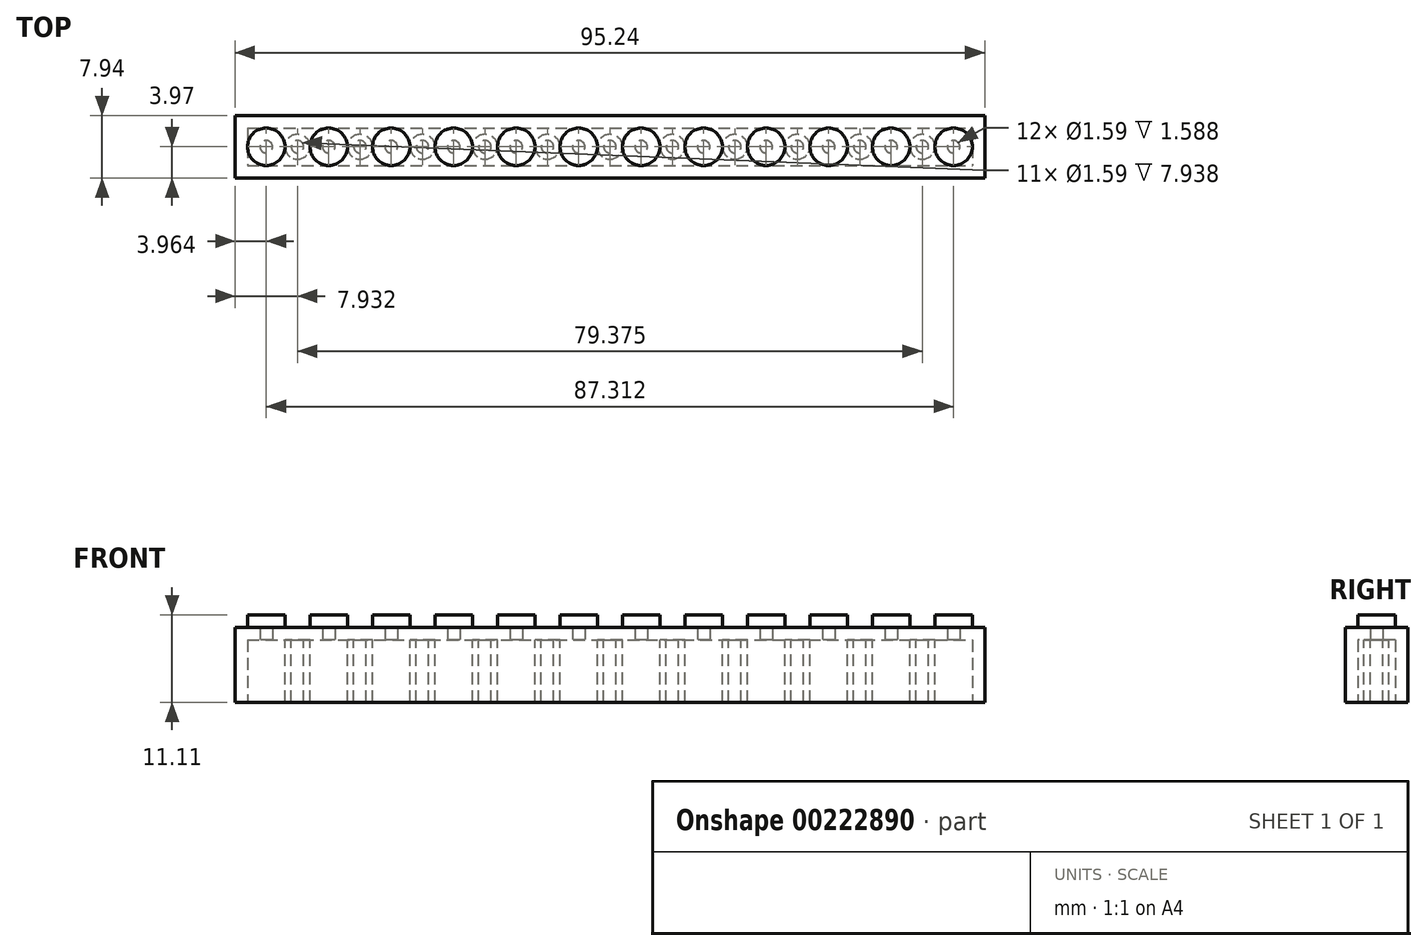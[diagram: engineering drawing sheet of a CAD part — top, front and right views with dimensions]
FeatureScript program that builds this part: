
annotation { "Feature Type Name" : "Feature", "Feature Type Description" : "" }
export const myFeature = defineFeature(function(context is Context, id is Id, definition is map)
    precondition{}
    {
        {
            var Q0;
            Q0=qCreatedBy(makeId("Top.planeOp"),FACE);
            var sketch = newSketch(context, id + "F0", { "sketchPlane" : qUnion([Q0])});
            skLineSegment(sketch, "E0.bottom", {"start": v(-47.63, 3.97) * mm, "end": v(47.62, 3.97) * mm});
            skLineSegment(sketch, "E0.top", {"start": v(-47.63, -3.97) * mm, "end": v(47.63, -3.97) * mm});
            skLineSegment(sketch, "E0.left", {"start": v(-47.63, 3.97) * mm, "end": v(-47.63, -3.97) * mm});
            skLineSegment(sketch, "E0.right", {"start": v(47.62, 3.97) * mm, "end": v(47.62, -3.97) * mm});
            skPoint(sketch, "E0.middle", {"position": v(0, 0) * mm});
            skCircle(sketch, "E1", {"center": v(-43.66, 0) * mm, "radius": 2.38 * mm});
            skCircle(sketch, "E2.1.0.0", {"center": v(-35.72, 0) * mm, "radius": 2.38 * mm});
            skCircle(sketch, "E2.2.0.0", {"center": v(-27.78, 0) * mm, "radius": 2.38 * mm});
            skCircle(sketch, "E2.3.0.0", {"center": v(-19.84, 0) * mm, "radius": 2.38 * mm});
            skLineSegment(sketch, "E2.direction1", {"start": v(-43.66, 0) * mm, "end": v(-35.72, 0) * mm, "construction": true});
            skCircle(sketch, "E3.0.4.0", {"center": v(-11.9, 0) * mm, "radius": 2.38 * mm});
            skCircle(sketch, "E3.0.5.0", {"center": v(-3.97, 0) * mm, "radius": 2.38 * mm});
            skCircle(sketch, "E4.0.6.0", {"center": v(3.97, 0) * mm, "radius": 2.38 * mm});
            skCircle(sketch, "E4.0.7.0", {"center": v(11.9, 0) * mm, "radius": 2.38 * mm});
            skCircle(sketch, "E4.0.8.0", {"center": v(19.84, 0) * mm, "radius": 2.38 * mm});
            skCircle(sketch, "E4.0.9.0", {"center": v(27.78, 0) * mm, "radius": 2.38 * mm});
            skCircle(sketch, "E4.0.10.0", {"center": v(35.72, 0) * mm, "radius": 2.38 * mm});
            skCircle(sketch, "E4.0.11.0", {"center": v(43.66, 0) * mm, "radius": 2.38 * mm});
            skSolve(sketch);
        }
        {
            var Q0;
            Q0=makeQuery(id+"F0.imprint","IMPRINT",FACE,{"disambiguationData":[TD([[makeQuery(id+"F0.imprint","IMPRINT",EDGE,{"derivedFrom":sQuery(id+"F0.wireOp",EDGE,"E0.bottom")}),-1.0]])]});
            extrude(context, id + "F1", {"entities" : qUnion([Q0]), "depth" : 9.52 * mm});
        }
        {
            var Q0;
            Q0=makeQuery(id+"F0.imprint","IMPRINT",FACE,{"disambiguationData":[TD([[makeQuery(id+"F0.imprint","IMPRINT",EDGE,{"derivedFrom":sQuery(id+"F0.wireOp",EDGE,"8b71ed98-f0e1-4300-85cb-82ad82c44b3e0.MirrorC")}),-1.0]])]});
            var Q1;
            Q1=makeQuery(id+"F0.imprint","IMPRINT",FACE,{"disambiguationData":[TD([[makeQuery(id+"F0.imprint","IMPRINT",EDGE,{"derivedFrom":sQuery(id+"F0.wireOp",EDGE,"E1")}),1.0]])]});
            var Q2;
            Q2=makeQuery(id+"F0.imprint","IMPRINT",FACE,{"disambiguationData":[TD([[makeQuery(id+"F0.imprint","IMPRINT",EDGE,{"derivedFrom":sQuery(id+"F0.wireOp",EDGE,"E2.1.0.0")}),1.0]])]});
            var Q3;
            Q3=makeQuery(id+"F0.imprint","IMPRINT",FACE,{"disambiguationData":[TD([[makeQuery(id+"F0.imprint","IMPRINT",EDGE,{"derivedFrom":sQuery(id+"F0.wireOp",EDGE,"E2.2.0.0")}),1.0]])]});
            var Q4;
            Q4=makeQuery(id+"F0.imprint","IMPRINT",FACE,{"disambiguationData":[TD([[makeQuery(id+"F0.imprint","IMPRINT",EDGE,{"derivedFrom":sQuery(id+"F0.wireOp",EDGE,"E2.3.0.0")}),1.0]])]});
            var Q5;
            Q5=makeQuery(id+"F0.imprint","IMPRINT",FACE,{"disambiguationData":[TD([[makeQuery(id+"F0.imprint","IMPRINT",EDGE,{"derivedFrom":sQuery(id+"F0.wireOp",EDGE,"E3.0.4.0")}),1.0]])]});
            var Q6;
            Q6=makeQuery(id+"F0.imprint","IMPRINT",FACE,{"disambiguationData":[TD([[makeQuery(id+"F0.imprint","IMPRINT",EDGE,{"derivedFrom":sQuery(id+"F0.wireOp",EDGE,"E3.0.5.0")}),1.0]])]});
            var Q7;
            Q7=makeQuery(id+"F0.imprint","IMPRINT",FACE,{"disambiguationData":[TD([[makeQuery(id+"F0.imprint","IMPRINT",EDGE,{"derivedFrom":sQuery(id+"F0.wireOp",EDGE,"E4.0.6.0")}),1.0]])]});
            var Q8;
            Q8=makeQuery(id+"F0.imprint","IMPRINT",FACE,{"disambiguationData":[TD([[makeQuery(id+"F0.imprint","IMPRINT",EDGE,{"derivedFrom":sQuery(id+"F0.wireOp",EDGE,"E4.0.7.0")}),1.0]])]});
            var Q9;
            Q9=makeQuery(id+"F0.imprint","IMPRINT",FACE,{"disambiguationData":[TD([[makeQuery(id+"F0.imprint","IMPRINT",EDGE,{"derivedFrom":sQuery(id+"F0.wireOp",EDGE,"E4.0.8.0")}),1.0]])]});
            var Q10;
            Q10=makeQuery(id+"F0.imprint","IMPRINT",FACE,{"disambiguationData":[TD([[makeQuery(id+"F0.imprint","IMPRINT",EDGE,{"derivedFrom":sQuery(id+"F0.wireOp",EDGE,"E4.0.9.0")}),1.0]])]});
            var Q11;
            Q11=makeQuery(id+"F0.imprint","IMPRINT",FACE,{"disambiguationData":[TD([[makeQuery(id+"F0.imprint","IMPRINT",EDGE,{"derivedFrom":sQuery(id+"F0.wireOp",EDGE,"E4.0.10.0")}),1.0]])]});
            var Q12;
            Q12=makeQuery(id+"F0.imprint","IMPRINT",FACE,{"disambiguationData":[TD([[makeQuery(id+"F0.imprint","IMPRINT",EDGE,{"derivedFrom":sQuery(id+"F0.wireOp",EDGE,"E4.0.11.0")}),1.0]])]});
            extrude(context, id + "F2", {"entities" : qUnion([Q0, Q1, Q2, Q3, Q4, Q5, Q6, Q7, Q8, Q9, Q10, Q11, Q12]), "operationType" : NewBodyOperationType.ADD, "depth" : 11.1 * mm});
        }
        {
            var Q0;
            {var subQ0=sQuery(id+"F0.wireOp",EDGE,"8b71ed98-f0e1-4300-85cb-82ad82c44b3e0.MirrorC");var subQ1=sQuery(id+"F0.wireOp",EDGE,"E1");Q0=makeQuery(id+"F2.boolean.opBoolean","MERGE",FACE,{"derivedFrom":[makeQuery(id+"F1.opExtrude","CAP_FACE",FACE,{"disambiguationData":[OSD([sQuery(id+"F0.wireOp",EDGE,"E0.bottom"),sQuery(id+"F0.wireOp",EDGE,"E0.top"),sQuery(id+"F0.wireOp",EDGE,"E0.left"),sQuery(id+"F0.wireOp",EDGE,"E0.right"),subQ1,subQ0])],"isStart":true}),makeQuery(id+"F2.opExtrude","CAP_FACE",FACE,{"disambiguationData":[OSD([subQ1])],"isStart":true}),makeQuery(id+"F2.opExtrude","CAP_FACE",FACE,{"disambiguationData":[OSD([subQ0])],"isStart":true})]});}
            shell(context, id + "F3", {"entities" : qUnion([Q0]), "thickness" : 1.59 * mm});
        }
        {
            var Q0;
            Q0=makeQuery(id+"F3.opShell","OFFSET_FACE",FACE,{"disambiguationData":[OSD([sQuery(id+"F0.wireOp",EDGE,"E0.bottom"),sQuery(id+"F0.wireOp",EDGE,"E0.top"),sQuery(id+"F0.wireOp",EDGE,"E0.left"),sQuery(id+"F0.wireOp",EDGE,"E0.right"),sQuery(id+"F0.wireOp",EDGE,"E1"),sQuery(id+"F0.wireOp",EDGE,"8b71ed98-f0e1-4300-85cb-82ad82c44b3e0.MirrorC")])]});
            var sketch = newSketch(context, id + "F4", { "sketchPlane" : qUnion([Q0])});
            skCircle(sketch, "E5", {"center": v(-39.69, 0) * mm, "radius": 1.59 * mm});
            skCircle(sketch, "E6", {"center": v(-39.69, 0) * mm, "radius": 0.8 * mm});
            skLineSegment(sketch, "E7.direction1", {"start": v(-39.69, 0) * mm, "end": v(-31.75, 0) * mm, "construction": true});
            skCircle(sketch, "E8.0.1.0", {"center": v(-31.75, 0) * mm, "radius": 1.59 * mm});
            skCircle(sketch, "E8.2.1.0", {"center": v(-31.75, 0) * mm, "radius": 0.8 * mm});
            skCircle(sketch, "E8.0.2.0", {"center": v(-23.81, 0) * mm, "radius": 1.59 * mm});
            skCircle(sketch, "E8.2.2.0", {"center": v(-23.81, 0) * mm, "radius": 0.8 * mm});
            skCircle(sketch, "E8.0.3.0", {"center": v(-15.88, 0) * mm, "radius": 1.59 * mm});
            skCircle(sketch, "E8.2.3.0", {"center": v(-15.88, 0) * mm, "radius": 0.8 * mm});
            skCircle(sketch, "E8.0.4.0", {"center": v(-7.94, 0) * mm, "radius": 1.59 * mm});
            skCircle(sketch, "E8.2.4.0", {"center": v(-7.94, 0) * mm, "radius": 0.8 * mm});
            skCircle(sketch, "E8.0.5.0", {"center": v(0, 0) * mm, "radius": 1.59 * mm});
            skCircle(sketch, "E8.2.5.0", {"center": v(0, 0) * mm, "radius": 0.8 * mm});
            skCircle(sketch, "E8.0.6.0", {"center": v(7.94, 0) * mm, "radius": 1.59 * mm});
            skCircle(sketch, "E8.2.6.0", {"center": v(7.94, 0) * mm, "radius": 0.8 * mm});
            skCircle(sketch, "E8.0.7.0", {"center": v(15.87, 0) * mm, "radius": 1.59 * mm});
            skCircle(sketch, "E8.2.7.0", {"center": v(15.87, 0) * mm, "radius": 0.8 * mm});
            skCircle(sketch, "E8.0.8.0", {"center": v(23.81, 0) * mm, "radius": 1.59 * mm});
            skCircle(sketch, "E8.2.8.0", {"center": v(23.81, 0) * mm, "radius": 0.8 * mm});
            skCircle(sketch, "E8.0.9.0", {"center": v(31.75, 0) * mm, "radius": 1.59 * mm});
            skCircle(sketch, "E8.2.9.0", {"center": v(31.75, 0) * mm, "radius": 0.8 * mm});
            skCircle(sketch, "E8.0.10.0", {"center": v(39.69, 0) * mm, "radius": 1.59 * mm});
            skCircle(sketch, "E8.2.10.0", {"center": v(39.69, 0) * mm, "radius": 0.8 * mm});
            skSolve(sketch);
        }
        {
            var Q0;
            Q0=makeQuery(id+"F4.imprint","IMPRINT",FACE,{"disambiguationData":[TD([[makeQuery(id+"F4.imprint","IMPRINT",EDGE,{"derivedFrom":sQuery(id+"F4.wireOp",EDGE,"E5")}),1.0]])]});
            var Q1;
            Q1=makeQuery(id+"F4.imprint","IMPRINT",FACE,{"disambiguationData":[TD([[makeQuery(id+"F4.imprint","IMPRINT",EDGE,{"derivedFrom":sQuery(id+"F4.wireOp",EDGE,"E7.1.0.0")}),1.0]])]});
            var Q2;
            Q2=makeQuery(id+"F4.imprint","IMPRINT",FACE,{"disambiguationData":[TD([[makeQuery(id+"F4.imprint","IMPRINT",EDGE,{"derivedFrom":sQuery(id+"F4.wireOp",EDGE,"E7.2.0.0")}),1.0]])]});
            var Q3;
            Q3=makeQuery(id+"F4.imprint","IMPRINT",FACE,{"disambiguationData":[TD([[makeQuery(id+"F4.imprint","IMPRINT",EDGE,{"derivedFrom":sQuery(id+"F4.wireOp",EDGE,"085d88cb-4c62-47cd-8297-15103481ccae.0.3.0")}),1.0]])]});
            var Q4;
            Q4=makeQuery(id+"F4.imprint","IMPRINT",FACE,{"disambiguationData":[TD([[makeQuery(id+"F4.imprint","IMPRINT",EDGE,{"derivedFrom":sQuery(id+"F4.wireOp",EDGE,"085d88cb-4c62-47cd-8297-15103481ccae.0.4.0")}),1.0]])]});
            var Q5;
            Q5=makeQuery(id+"F4.imprint","IMPRINT",FACE,{"disambiguationData":[TD([[makeQuery(id+"F4.imprint","IMPRINT",EDGE,{"derivedFrom":sQuery(id+"F4.wireOp",EDGE,"E8.0.1.0")}),1.0]])]});
            var Q6;
            Q6=makeQuery(id+"F4.imprint","IMPRINT",FACE,{"disambiguationData":[TD([[makeQuery(id+"F4.imprint","IMPRINT",EDGE,{"derivedFrom":sQuery(id+"F4.wireOp",EDGE,"E8.0.2.0")}),1.0]])]});
            var Q7;
            Q7=makeQuery(id+"F4.imprint","IMPRINT",FACE,{"disambiguationData":[TD([[makeQuery(id+"F4.imprint","IMPRINT",EDGE,{"derivedFrom":sQuery(id+"F4.wireOp",EDGE,"E8.0.3.0")}),1.0]])]});
            var Q8;
            Q8=makeQuery(id+"F4.imprint","IMPRINT",FACE,{"disambiguationData":[TD([[makeQuery(id+"F4.imprint","IMPRINT",EDGE,{"derivedFrom":sQuery(id+"F4.wireOp",EDGE,"E8.0.4.0")}),1.0]])]});
            var Q9;
            Q9=makeQuery(id+"F4.imprint","IMPRINT",FACE,{"disambiguationData":[TD([[makeQuery(id+"F4.imprint","IMPRINT",EDGE,{"derivedFrom":sQuery(id+"F4.wireOp",EDGE,"E8.0.5.0")}),1.0]])]});
            var Q10;
            Q10=makeQuery(id+"F4.imprint","IMPRINT",FACE,{"disambiguationData":[TD([[makeQuery(id+"F4.imprint","IMPRINT",EDGE,{"derivedFrom":sQuery(id+"F4.wireOp",EDGE,"E8.0.6.0")}),1.0]])]});
            var Q11;
            Q11=makeQuery(id+"F4.imprint","IMPRINT",FACE,{"disambiguationData":[TD([[makeQuery(id+"F4.imprint","IMPRINT",EDGE,{"derivedFrom":sQuery(id+"F4.wireOp",EDGE,"E8.0.7.0")}),1.0]])]});
            var Q12;
            Q12=makeQuery(id+"F4.imprint","IMPRINT",FACE,{"disambiguationData":[TD([[makeQuery(id+"F4.imprint","IMPRINT",EDGE,{"derivedFrom":sQuery(id+"F4.wireOp",EDGE,"E8.0.8.0")}),1.0]])]});
            var Q13;
            Q13=makeQuery(id+"F4.imprint","IMPRINT",FACE,{"disambiguationData":[TD([[makeQuery(id+"F4.imprint","IMPRINT",EDGE,{"derivedFrom":sQuery(id+"F4.wireOp",EDGE,"E8.0.9.0")}),1.0]])]});
            var Q14;
            Q14=makeQuery(id+"F4.imprint","IMPRINT",FACE,{"disambiguationData":[TD([[makeQuery(id+"F4.imprint","IMPRINT",EDGE,{"derivedFrom":sQuery(id+"F4.wireOp",EDGE,"E8.0.10.0")}),1.0]])]});
            extrude(context, id + "F5", {"entities" : qUnion([Q0, Q1, Q2, Q3, Q4, Q5, Q6, Q7, Q8, Q9, Q10, Q11, Q12, Q13, Q14]), "operationType" : NewBodyOperationType.ADD, "depth" : 7.94 * mm});
        }
    });
